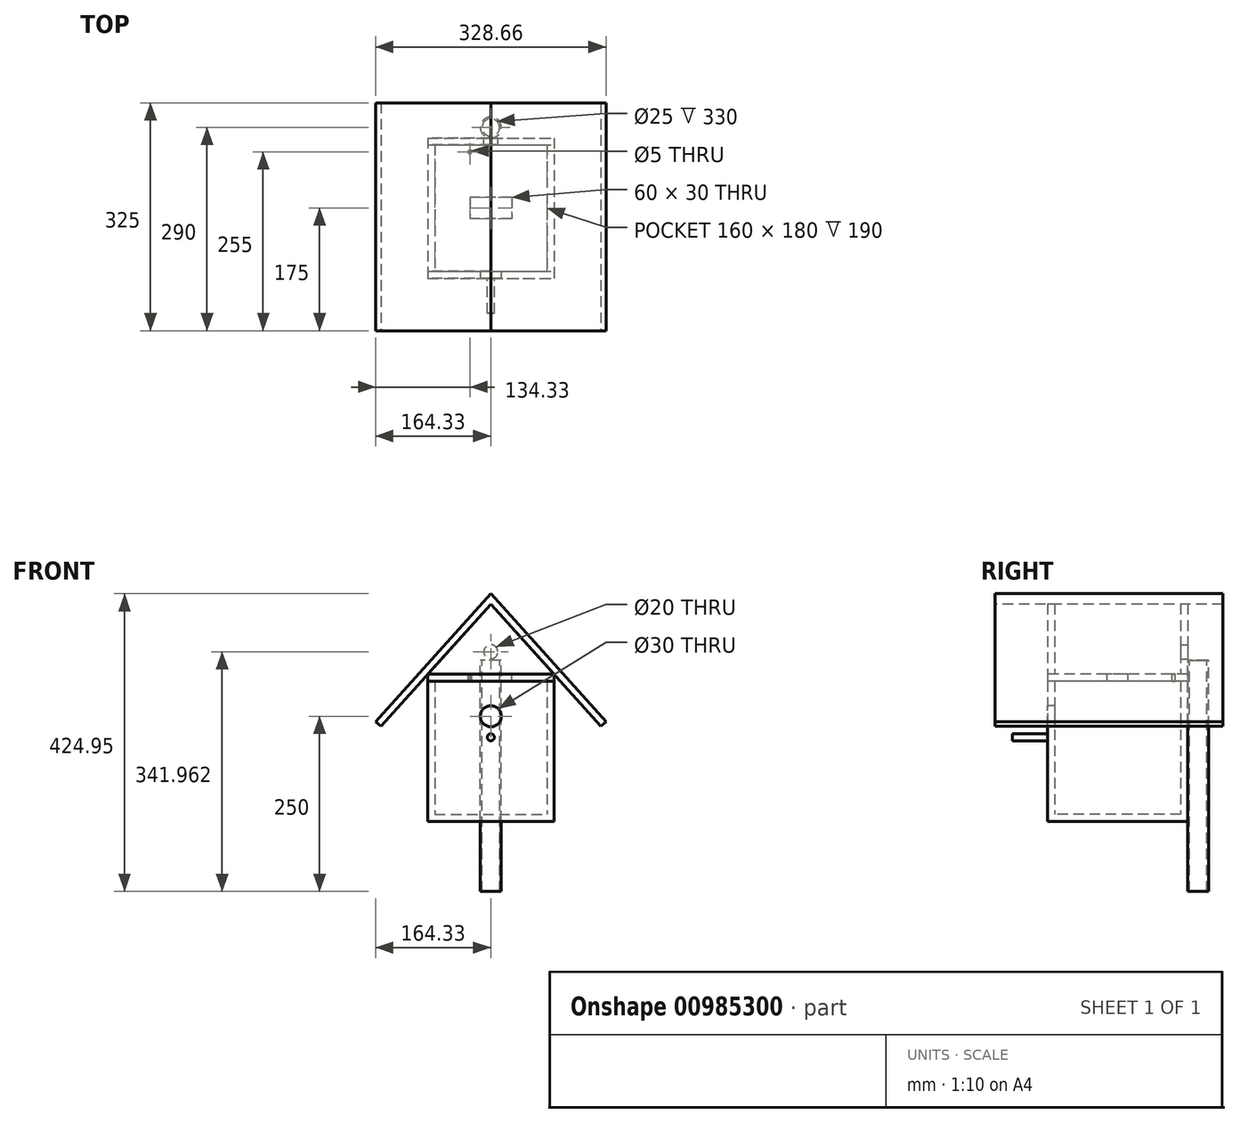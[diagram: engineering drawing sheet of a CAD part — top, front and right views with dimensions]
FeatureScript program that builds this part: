
annotation { "Feature Type Name" : "Feature", "Feature Type Description" : "" }
export const myFeature = defineFeature(function(context is Context, id is Id, definition is map)
    precondition{}
    {
        {
            var Q0;
            Q0=qCreatedBy(makeId("Top.planeOp"),FACE);
            var sketch = newSketch(context, id + "F0", { "sketchPlane" : qUnion([Q0])});
            skLineSegment(sketch, "E0.bottom", {"start": v(-90, 100) * mm, "end": v(90, 100) * mm});
            skLineSegment(sketch, "E0.top", {"start": v(-90, -100) * mm, "end": v(90, -100) * mm});
            skLineSegment(sketch, "E0.left", {"start": v(-90, 100) * mm, "end": v(-90, -100) * mm});
            skLineSegment(sketch, "E0.right", {"start": v(90, 100) * mm, "end": v(90, -100) * mm});
            skSolve(sketch);
        }
        {
            var Q0;
            Q0 = qSketchRegion(id + "F0", true);
            extrude(context, id + "F1", {"entities" : qUnion([Q0]), "depth" : 200 * mm, "offsetDistance" : 25 * mm});
        }
        {
            var Q0;
            Q0=makeQuery(id+"F1.opExtrude","CAP_FACE",FACE,{"disambiguationData":[OSD([sQuery(id+"F0.wireOp",EDGE,"E0.bottom"),sQuery(id+"F0.wireOp",EDGE,"E0.top"),sQuery(id+"F0.wireOp",EDGE,"E0.left"),sQuery(id+"F0.wireOp",EDGE,"E0.right")])],"isStart":false});
            shell(context, id + "F2", {"entities" : qUnion([Q0]), "thickness" : 10 * mm});
        }
        {
            var Q0;
            Q0=makeQuery(id+"F1.opExtrude","SWEPT_FACE",FACE,{"disambiguationData":[OSD([sQuery(id+"F0.wireOp",EDGE,"E0.top")])]});
            var sketch = newSketch(context, id + "F3", { "sketchPlane" : qUnion([Q0])});
            skCircle(sketch, "E1", {"center": v(0, 120) * mm, "radius": 5 * mm});
            skPoint(sketch, "E1.centerSnap0", {"position": v(0, 0) * mm});
            skCircle(sketch, "E2", {"center": v(0, 150) * mm, "radius": 15 * mm});
            skSolve(sketch);
        }
        {
            var Q0;
            Q0=makeQuery(id+"F3.imprint","IMPRINT",FACE,{"disambiguationData":[TD([[makeQuery(id+"F3.imprint","IMPRINT",EDGE,{"derivedFrom":sQuery(id+"F3.wireOp",EDGE,"E2")}),1.0]])]});
            extrude(context, id + "F4", {"entities" : qUnion([Q0]), "operationType" : NewBodyOperationType.REMOVE, "oppositeDirection" : true, "depth" : 25 * mm, "offsetDistance" : 25 * mm});
        }
        {
            var Q0;
            Q0=makeQuery(id+"F3.imprint","IMPRINT",FACE,{"disambiguationData":[TD([[makeQuery(id+"F3.imprint","IMPRINT",EDGE,{"derivedFrom":sQuery(id+"F3.wireOp",EDGE,"E1")}),1.0]])]});
            extrude(context, id + "F5", {"entities" : qUnion([Q0]), "operationType" : NewBodyOperationType.ADD, "depth" : 50 * mm, "offsetDistance" : 25 * mm});
        }
        {
            var Q0;
            Q0=makeQuery(id+"F1.opExtrude","CAP_FACE",FACE,{"disambiguationData":[OSD([sQuery(id+"F0.wireOp",EDGE,"E0.bottom"),sQuery(id+"F0.wireOp",EDGE,"E0.top"),sQuery(id+"F0.wireOp",EDGE,"E0.left"),sQuery(id+"F0.wireOp",EDGE,"E0.right")])],"isStart":false});
            var sketch = newSketch(context, id + "F6", { "sketchPlane" : qUnion([Q0])});
            skCircle(sketch, "E3", {"center": v(0, 115) * mm, "radius": 15 * mm});
            skPoint(sketch, "E3.centerSnap0", {"position": v(0, 100) * mm});
            skSolve(sketch);
        }
        {
            var Q0;
            Q0=makeQuery(id+"F6.imprint","IMPRINT",FACE,{"disambiguationData":[TD([[makeQuery(id+"F6.imprint","IMPRINT",EDGE,{"derivedFrom":sQuery(id+"F6.wireOp",EDGE,"E3")}),1.0]])]});
            var Q1;
            Q1=sQuery(id+"F6.wireOp",EDGE,"E3");
            extrude(context, id + "F7", {"entities" : qUnion([Q0]), "operationType" : NewBodyOperationType.ADD, "surfaceEntities" : qUnion([Q1]), "oppositeDirection" : true, "depth" : 300 * mm, "offsetDistance" : 25 * mm, "hasSecondDirection" : true, "secondDirectionOppositeDirection" : false, "secondDirectionDepth" : 30 * mm});
        }
        {
            var Q0;
            Q0=makeQuery(id+"F1.opExtrude","CAP_FACE",FACE,{"disambiguationData":[OSD([sQuery(id+"F0.wireOp",EDGE,"E0.bottom"),sQuery(id+"F0.wireOp",EDGE,"E0.top"),sQuery(id+"F0.wireOp",EDGE,"E0.left"),sQuery(id+"F0.wireOp",EDGE,"E0.right")])],"isStart":false});
            var sketch = newSketch(context, id + "F8", { "sketchPlane" : qUnion([Q0])});
            skSolve(sketch);
        }
        {
            var Q0;
            {var subQ0=sQuery(id+"F0.wireOp",EDGE,"E0.bottom");Q0=makeQuery(id+"F8.imprint","IMPRINT",FACE,{"disambiguationData":[TD([[makeQuery(id+"F8.imprint","IMPRINT",EDGE,{"derivedFrom":makeQuery(id+"F2.opShell","OFFSET_EDGE",EDGE,{"disambiguationData":[OSD([subQ0]),TDD([makeQuery(id+"F1.opExtrude","CAP_EDGE",EDGE,{"disambiguationData":[OSD([subQ0])],"isStart":false})])]})}),-1.0]])]});}
            var Q1;
            {var subQ6=sQuery(id+"F0.wireOp",EDGE,"E0.bottom");var subQ7=makeQuery(id+"F1.opExtrude","CAP_EDGE",EDGE,{"disambiguationData":[OSD([subQ6])],"isStart":false});Q1=makeQuery(id+"F8.imprint","IMPRINT",FACE,{"disambiguationData":[TD([[makeQuery(id+"F8.imprint","IMPRINT",EDGE,{"derivedFrom":subQ7}),-1.0]])]});}
            extrude(context, id + "F9", {"entities" : qUnion([Q0, Q1]), "depth" : 10 * mm, "offsetDistance" : 25 * mm});
        }
        {
            var Q0;
            Q0=makeQuery(id+"F9.opExtrude","SWEPT_FACE",FACE,{"disambiguationData":[OSD([sQuery(id+"F0.wireOp",EDGE,"E0.top")])]});
            var sketch = newSketch(context, id + "F10", { "sketchPlane" : qUnion([Q0])});
            skLineSegment(sketch, "E4", {"start": v(0, 210) * mm, "end": v(0, 310) * mm, "construction": true});
            skLineSegment(sketch, "E5", {"start": v(0, 310) * mm, "end": v(-90, 210) * mm});
            skLineSegment(sketch, "E6", {"start": v(-90, 210) * mm, "end": v(-156.9, 135.67) * mm});
            skLineSegment(sketch, "E7.0", {"start": v(-97.43, 216.69) * mm, "end": v(-164.33, 142.36) * mm});
            skLineSegment(sketch, "E7.1", {"start": v(-7.43, 316.69) * mm, "end": v(-97.43, 216.69) * mm});
            skLineSegment(sketch, "E8.MirrorCS", {"start": v(7.43, 316.69) * mm, "end": v(97.43, 216.69) * mm});
            skLineSegment(sketch, "E9.MirrorCS", {"start": v(0, 310) * mm, "end": v(90, 210) * mm});
            skLineSegment(sketch, "E10.MirrorCS", {"start": v(97.43, 216.69) * mm, "end": v(164.33, 142.36) * mm});
            skLineSegment(sketch, "E11.MirrorCS", {"start": v(90, 210) * mm, "end": v(156.9, 135.67) * mm});
            skLineSegment(sketch, "E12", {"start": v(-7.43, 316.69) * mm, "end": v(0, 324.95) * mm});
            skLineSegment(sketch, "E13", {"start": v(7.43, 316.69) * mm, "end": v(0, 324.95) * mm});
            skLineSegment(sketch, "E14", {"start": v(156.9, 135.67) * mm, "end": v(164.33, 142.36) * mm});
            skLineSegment(sketch, "E15", {"start": v(-156.9, 135.67) * mm, "end": v(-164.33, 142.36) * mm});
            skSolve(sketch);
        }
        {
            var Q0;
            Q0=makeQuery(id+"F10.imprint","IMPRINT",FACE,{"disambiguationData":[TD([[makeQuery(id+"F10.imprint","IMPRINT",EDGE,{"derivedFrom":sQuery(id+"F10.wireOp",EDGE,"E5")}),-1.0]])]});
            extrude(context, id + "F11", {"entities" : qUnion([Q0]), "oppositeDirection" : true, "depth" : 250 * mm, "offsetDistance" : 25 * mm, "hasSecondDirection" : true, "secondDirectionOppositeDirection" : false, "secondDirectionDepth" : 75 * mm});
        }
        {
            var Q0;
            Q0=makeQuery(id+"F10.imprint","IMPRINT",FACE,{"disambiguationData":[TD([[makeQuery(id+"F10.imprint","IMPRINT",EDGE,{"derivedFrom":sQuery(id+"F10.wireOp",EDGE,"E5")}),1.0]])]});
            extrude(context, id + "F12", {"entities" : qUnion([Q0]), "oppositeDirection" : true, "depth" : 10 * mm, "offsetDistance" : 25 * mm});
        }
        {
            var Q0;
            Q0=makeQuery(id+"F10.imprint","IMPRINT",FACE,{"disambiguationData":[TD([[makeQuery(id+"F10.imprint","IMPRINT",EDGE,{"derivedFrom":sQuery(id+"F10.wireOp",EDGE,"E5")}),1.0]])]});
            extrude(context, id + "F13", {"entities" : qUnion([Q0]), "oppositeDirection" : true, "depth" : 200 * mm, "offsetDistance" : 25 * mm, "hasSecondDirection" : true, "secondDirectionOppositeDirection" : true, "secondDirectionDepth" : 190 * mm});
        }
        {
            var Q0;
            Q0=makeQuery(id+"F13.opExtrude","CAP_FACE",FACE,{"disambiguationData":[OSD([sQuery(id+"F0.wireOp",EDGE,"E0.top"),sQuery(id+"F10.wireOp",EDGE,"E5"),sQuery(id+"F10.wireOp",EDGE,"E9.MirrorCS")])],"isStart":false});
            var sketch = newSketch(context, id + "F14", { "sketchPlane" : qUnion([Q0])});
            skCircle(sketch, "E16", {"center": v(0, 241.96) * mm, "radius": 10 * mm});
            skSolve(sketch);
        }
        {
            var Q0;
            Q0 = qSketchRegion(id + "F14", true);
            extrude(context, id + "F15", {"entities" : qUnion([Q0]), "operationType" : NewBodyOperationType.REMOVE, "oppositeDirection" : true, "depth" : 10 * mm, "offsetDistance" : 25 * mm});
        }
        {
            var Q0;
            Q0=makeQuery(id+"F9.opExtrude","CAP_FACE",FACE,{"disambiguationData":[OSD([sQuery(id+"F0.wireOp",EDGE,"E0.bottom"),sQuery(id+"F0.wireOp",EDGE,"E0.top"),sQuery(id+"F0.wireOp",EDGE,"E0.left"),sQuery(id+"F0.wireOp",EDGE,"E0.right")])],"isStart":false});
            var sketch = newSketch(context, id + "F16", { "sketchPlane" : qUnion([Q0])});
            skLineSegment(sketch, "E17", {"start": v(0, 15) * mm, "end": v(0, 0) * mm, "construction": true});
            skLineSegment(sketch, "E18", {"start": v(0, 15) * mm, "end": v(30, 15) * mm, "construction": true});
            skLineSegment(sketch, "E19.bottom", {"start": v(30, 15) * mm, "end": v(-30, 15) * mm});
            skLineSegment(sketch, "E19.top", {"start": v(30, -15) * mm, "end": v(-30, -15) * mm});
            skLineSegment(sketch, "E19.left", {"start": v(30, 15) * mm, "end": v(30, -15) * mm});
            skLineSegment(sketch, "E19.right", {"start": v(-30, 15) * mm, "end": v(-30, -15) * mm});
            skCircle(sketch, "E20", {"center": v(-30, 80) * mm, "radius": 2.5 * mm});
            skSolve(sketch);
        }
        {
            var Q0;
            Q0=makeQuery(id+"F16.imprint","IMPRINT",FACE,{"disambiguationData":[TD([[makeQuery(id+"F16.imprint","IMPRINT",EDGE,{"derivedFrom":sQuery(id+"F16.wireOp",EDGE,"E19.bottom")}),1.0]])]});
            var Q1;
            Q1=makeQuery(id+"F16.imprint","IMPRINT",FACE,{"disambiguationData":[TD([[makeQuery(id+"F16.imprint","IMPRINT",EDGE,{"derivedFrom":sQuery(id+"F16.wireOp",EDGE,"E20")}),1.0]])]});
            extrude(context, id + "F17", {"entities" : qUnion([Q0, Q1]), "operationType" : NewBodyOperationType.REMOVE, "oppositeDirection" : true, "depth" : 25 * mm, "offsetDistance" : 25 * mm});
        }
        {
            var Q0;
            Q0=makeQuery(id+"F7.opExtrude","CAP_FACE",FACE,{"disambiguationData":[OSD([sQuery(id+"F6.wireOp",EDGE,"E3")])],"isStart":true});
            shell(context, id + "F18", {"entities" : qUnion([Q0]), "thickness" : 2.5 * mm});
        }
        {
            var Q0;
            {var subQ0=sQuery(id+"F6.wireOp",EDGE,"E3");Q0=makeQuery(id+"F18.opShell","OFFSET_FACE",FACE,{"disambiguationData":[OSD([subQ0]),TDD([makeQuery(id+"F7.opExtrude","CAP_FACE",FACE,{"disambiguationData":[OSD([subQ0])],"isStart":false})])]});}
            extrude(context, id + "F19", {"entities" : qUnion([Q0]), "operationType" : NewBodyOperationType.REMOVE, "oppositeDirection" : true, "depth" : 25 * mm, "offsetDistance" : 25 * mm});
        }
    });
